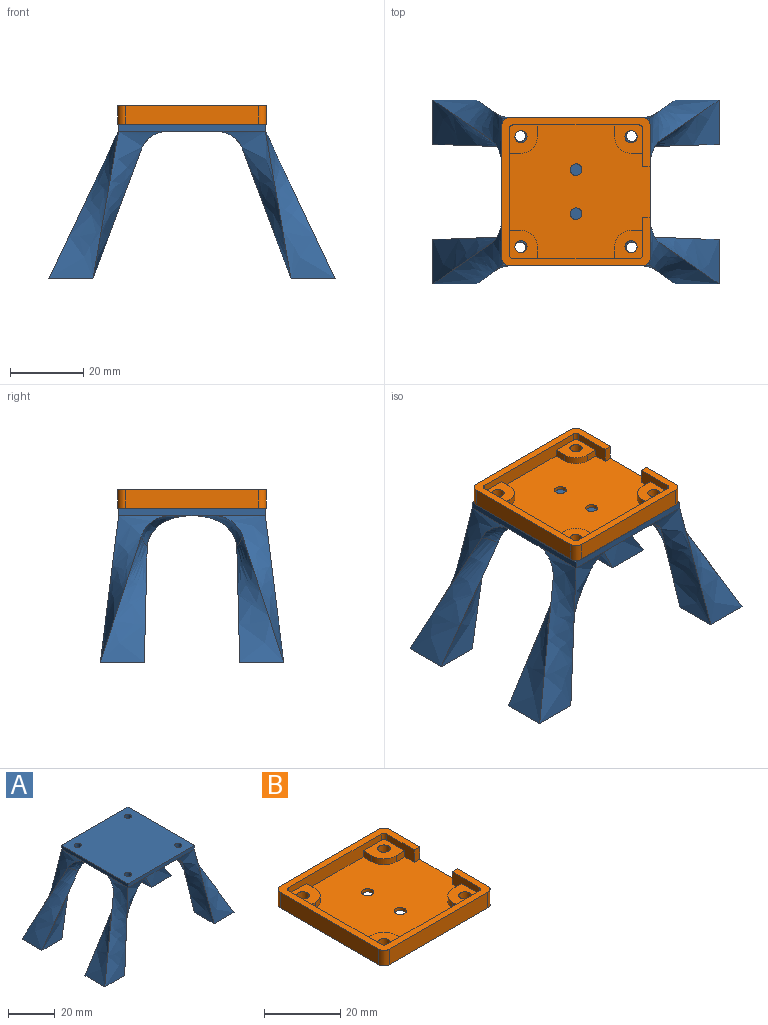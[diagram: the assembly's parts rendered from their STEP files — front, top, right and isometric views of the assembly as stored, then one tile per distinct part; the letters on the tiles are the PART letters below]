
ASSEMBLY  parts=2 mates=1
PART A: 40 faces, bbox 97x50x42 mm
  f0: plane 40x18.73mm, normal (0,0,-1), area 668.7mm2, adj f6,f8,f32,f33,f36,f37
  f1: plane 11.5x9.93mm, normal (0,0,-1), area 60.8mm2, adj f7,f34,f35
  f2: bspline ~40x32.21mm, area 303.4mm2, adj f16,f18,f19,f31,f37,f39
  f3: bspline ~40x32.21mm, area 307.7mm2, adj f20,f21,f22,f30,f32,f34
  f4: bspline ~40x32.21mm, area 307.7mm2, adj f24,f26,f27,f29,f33,f35
  f5: bspline ~40x32.21mm, area 303.4mm2, adj f12,f13,f14,f28,f36,f38
  f6: plane 40x2mm, normal (0,-1,0), area 80mm2, adj f0,f7,f9,f10,f18,f22
  f7: plane 40x2mm, normal (1,0,0), area 80mm2, adj f1,f6,f8,f10,f23,f25
  f8: plane 40x2mm, normal (0,1,0), area 80mm2, adj f0,f7,f9,f10,f14,f26
  f9: plane 40x2mm, normal (-1,0,0), area 80mm2, adj f6,f8,f10,f11,f15,f17
  f10: plane 40x40mm, normal (0,0,1), area 1571.7mm2, adj f6,f7,f8,f9,f28,f29,f30,f31
  f11: plane 11.5x9.93mm, normal (0,0,-1), area 60.8mm2, adj f9,f38,f39
  f12: plane 12x12mm, normal (0,0,-1), area 144mm2, adj f5,f13,f14,f15
  f13: bspline ~40x27mm, area 301.5mm2, adj f5,f12,f15,f38
  f14: bspline ~40x20.28mm, area 349.1mm2, adj f5,f8,f12,f15,f36
  f15: bspline ~40x28.51mm, area 364.8mm2, adj f9,f12,f13,f14,f38
  f16: plane 12x12mm, normal (0,0,-1), area 144mm2, adj f2,f17,f18,f19
  f17: bspline ~40x28.51mm, area 364.8mm2, adj f9,f16,f18,f19,f39
  f18: bspline ~40x20.28mm, area 349.1mm2, adj f2,f6,f16,f17,f37
  f19: bspline ~40x27mm, area 301.5mm2, adj f2,f16,f17,f39
  f20: plane 12x12mm, normal (0,0,-1), area 144mm2, adj f3,f21,f22,f23
  f21: bspline ~40x27mm, area 301.5mm2, adj f3,f20,f23,f34
  f22: bspline ~40x20.28mm, area 349.1mm2, adj f3,f6,f20,f23,f32
  f23: bspline ~40x28.51mm, area 364.8mm2, adj f7,f20,f21,f22,f34
  f24: plane 12x12mm, normal (0,0,-1), area 144mm2, adj f4,f25,f26,f27
  f25: bspline ~40x28.51mm, area 364.8mm2, adj f7,f24,f26,f27,f35
  f26: bspline ~40x20.28mm, area 349.1mm2, adj f4,f8,f24,f25,f33
  f27: bspline ~40x27mm, area 301.5mm2, adj f4,f24,f25,f35
  f28: cylinder r=1.5mm len=11.13mm, axis (0,0,1), area 75.8mm2, adj f5,f10,f36
  f29: cylinder r=1.5mm len=11.13mm, axis (0,0,1), area 76.4mm2, adj f4,f10,f33
  f30: cylinder r=1.5mm len=11.13mm, axis (0,0,1), area 76.4mm2, adj f3,f10,f32
  f31: cylinder r=1.5mm len=11.13mm, axis (0,0,1), area 75.8mm2, adj f2,f10,f37
  f32: bspline ~28.33x7.81mm, area 106.7mm2, adj f0,f3,f22,f30,f33,f34
  f33: bspline ~28.33x7.81mm, area 106.7mm2, adj f0,f4,f26,f29,f32,f35
  f34: bspline ~28.65x17.77mm, area 95.6mm2, adj f1,f3,f21,f23,f32,f35
  f35: bspline ~28.65x17.77mm, area 95.6mm2, adj f1,f4,f25,f27,f33,f34
  f36: bspline ~28.33x7.81mm, area 106.7mm2, adj f0,f5,f14,f28,f37,f38
  f37: bspline ~28.33x7.81mm, area 106.7mm2, adj f0,f2,f18,f31,f36,f39
  f38: bspline ~28.65x17.77mm, area 95.6mm2, adj f5,f11,f13,f15,f36,f39
  f39: bspline ~28.65x17.77mm, area 95.6mm2, adj f2,f11,f17,f19,f37,f38
PART B: 44 faces, bbox 40.4x40.4x5 mm
  f0: plane 34.4x4mm, normal (0,-1,0), area 110.8mm2, adj f2,f19,f30,f31,f32,f35,f42,f43
  f1: plane 34.4x4mm, normal (1,0,0), area 110.8mm2, adj f2,f19,f22,f23,f28,f31,f41,f42
  f2: plane 38.4x36.4mm, normal (0,0,1), area 1117.4mm2, adj f0,f1,f4,f7,f8,f14,f15,f16
  f3: plane 36.4x5mm, normal (0,-1,0), area 182mm2, adj f13,f19,f38,f39
  f4: plane 36.4x5mm, normal (1,0,0), area 126mm2, adj f2,f13,f15,f16,f19,f36,f39
  f5: plane 36.4x5mm, normal (0,1,0), area 182mm2, adj f13,f19,f36,f37
  f6: cylinder r=1.65mm len=3.3mm, axis (0,0,-1), area 31.1mm2, adj f13,f35
  f7: cylinder r=1.6mm len=3.2mm, axis (0,0,-1), area 10.1mm2, adj f2,f13
  f8: cylinder r=1.6mm len=3.2mm, axis (0,0,-1), area 10.1mm2, adj f2,f13
  f9: plane 36.4x5mm, normal (-1,0,0), area 182mm2, adj f13,f19,f37,f38
  f10: cylinder r=1.65mm len=3.3mm, axis (0,0,-1), area 31.1mm2, adj f13,f27
  f11: cylinder r=1.65mm len=3.3mm, axis (0,0,-1), area 31.1mm2, adj f13,f23
  f12: cylinder r=1.65mm len=3.3mm, axis (0,0,-1), area 31.1mm2, adj f13,f31
  f13: plane 40.4x40.4mm, normal (0,0,-1), area 1578.4mm2, adj f3,f4,f5,f6,f7,f8,f9,f10
  f14: plane 10.2x4mm, normal (-1,0,0), area 27.4mm2, adj f2,f15,f19,f34,f35,f43
  f15: plane 4x2mm, normal (0,-1,0), area 8mm2, adj f2,f4,f14,f19
  f16: plane 4x2mm, normal (0,1,0), area 8mm2, adj f2,f4,f17,f19
  f17: plane 10.2x4mm, normal (-1,0,0), area 27.4mm2, adj f2,f16,f19,f26,f27,f40
  f18: plane 34.4x4mm, normal (0,1,0), area 110.8mm2, adj f2,f19,f20,f23,f25,f27,f40,f41
  f19: plane 40.4x40.4mm, normal (0,0,1), area 276.6mm2, adj f0,f1,f3,f4,f5,f9,f14,f15
  f20: plane 3.2x2mm, normal (1,0,0), area 6.4mm2, adj f2,f18,f21,f23
  f21: cylinder r=4.5mm len=4.5mm, axis (0,0,-1), area 14.1mm2, adj f2,f20,f22,f23
  f22: plane 3.2x2mm, normal (0,1,0), area 6.4mm2, adj f1,f2,f21,f23
  f23: plane 7.7x7.7mm, normal (0,0,1), area 46.1mm2, adj f1,f11,f18,f20,f21,f22,f41
  f24: cylinder r=4.5mm len=4.5mm, axis (0,0,-1), area 14.1mm2, adj f2,f25,f26,f27
  f25: plane 3.2x2mm, normal (-1,0,0), area 6.4mm2, adj f2,f18,f24,f27
  f26: plane 3.2x2mm, normal (0,1,0), area 6.4mm2, adj f2,f17,f24,f27
  f27: plane 7.7x7.7mm, normal (0,0,1), area 46.1mm2, adj f10,f17,f18,f24,f25,f26,f40
  f28: plane 3.2x2mm, normal (0,-1,0), area 6.4mm2, adj f1,f2,f29,f31
  f29: cylinder r=4.5mm len=4.5mm, axis (0,0,-1), area 14.1mm2, adj f2,f28,f30,f31
  f30: plane 3.2x2mm, normal (1,0,0), area 6.4mm2, adj f0,f2,f29,f31
  f31: plane 7.7x7.7mm, normal (0,0,1), area 46.1mm2, adj f0,f1,f12,f28,f29,f30,f42
  f32: plane 3.2x2mm, normal (-1,0,0), area 6.4mm2, adj f0,f2,f33,f35
  f33: cylinder r=4.5mm len=4.5mm, axis (0,0,-1), area 14.1mm2, adj f2,f32,f34,f35
  f34: plane 3.2x2mm, normal (0,-1,0), area 6.4mm2, adj f2,f14,f33,f35
  f35: plane 7.7x7.7mm, normal (0,0,1), area 46.1mm2, adj f0,f6,f14,f32,f33,f34,f43
  f36: cylinder r=2mm len=5mm, axis (0,0,1), area 15.7mm2, adj f4,f5,f13,f19
  f37: cylinder r=2mm len=5mm, axis (0,0,-1), area 15.7mm2, adj f5,f9,f13,f19
  f38: cylinder r=2mm len=5mm, axis (0,0,1), area 15.7mm2, adj f3,f9,f13,f19
  f39: cylinder r=2mm len=5mm, axis (0,0,-1), area 15.7mm2, adj f3,f4,f13,f19
  f40: cylinder r=1mm len=2mm, axis (0,0,1), area 3.1mm2, adj f17,f18,f19,f27
  f41: cylinder r=1mm len=2mm, axis (0,0,-1), area 3.1mm2, adj f1,f18,f19,f23
  f42: cylinder r=1mm len=2mm, axis (0,0,1), area 3.1mm2, adj f0,f1,f19,f31
  f43: cylinder r=1mm len=2mm, axis (0,0,-1), area 3.1mm2, adj f0,f14,f19,f35
PLACE A t=(-9.56,-19.97,0.46)mm
PLACE B t=(-2.66,-33.73,42.46)mm
MATE planar B.f13 <-> A.f10  axis (0,0,-1) through (-9.56,-19.97,42.46)mm
